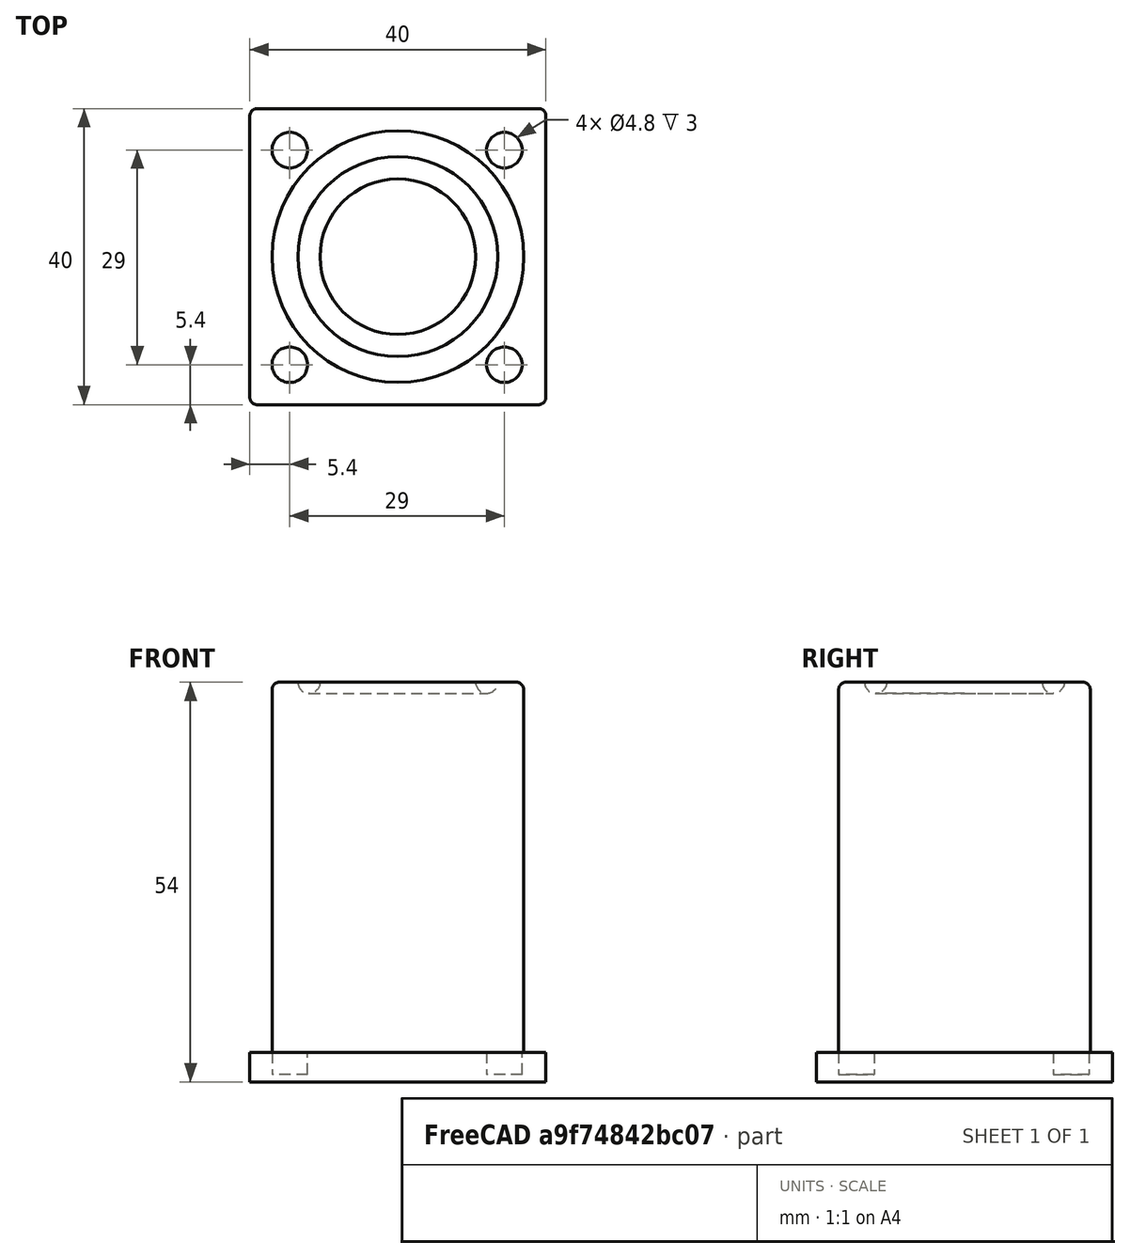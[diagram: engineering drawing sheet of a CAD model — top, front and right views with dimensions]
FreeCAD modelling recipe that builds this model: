
FCSTD DOCUMENT  (FreeCAD 1.0R39319 (Git))
Label: ojt1_t15r03_table_leg
License: All rights reserved
LicenseURL: https://en.wikipedia.org/wiki/All_rights_reserved
objects: Part::Cylinder×5, Part::Cut×2, Part::Fillet×2, Part::Box×1, Part::MultiFuse×1, Part::Torus×1
note: 12 computed .brp shape members not serialized (recipe doc carries the construction recipe); baked Part::Feature solids carry a one-line shape summary decoded from their .brp

FEATURE [Part::Box] Box  label="Cub"
  AttacherType = Attacher::AttachEngine3D
  Height = 4
  Length = 40
  Width = 40
FEATURE [Part::Cylinder] Cylinder  label="Cilindre"
  Angle = 360
  AttacherType = Attacher::AttachEngine3D
  FirstAngle = 0
  Height = 3
  Placement = pos=(5.4,5.4,1) rot=(0,0,1;0rad)
  Radius = 2.4
  SecondAngle = 0
FEATURE [Part::Cylinder] Cylinder001  label="Cilindre001"
  Angle = 360
  AttacherType = Attacher::AttachEngine3D
  FirstAngle = 0
  Height = 3
  Placement = pos=(34.4,5.4,1) rot=(0,0,1;0rad)
  Radius = 2.4
  SecondAngle = 0
FEATURE [Part::Cylinder] Cylinder002  label="Cilindre002"
  Angle = 360
  AttacherType = Attacher::AttachEngine3D
  FirstAngle = 0
  Height = 3
  Placement = pos=(34.4,34.4,1) rot=(0,0,1;0rad)
  Radius = 2.4
  SecondAngle = 0
FEATURE [Part::Cylinder] Cylinder003  label="Cilindre003"
  Angle = 360
  AttacherType = Attacher::AttachEngine3D
  FirstAngle = 0
  Height = 3
  Placement = pos=(5.4,34.4,1) rot=(0,0,1;0rad)
  Radius = 2.4
  SecondAngle = 0
FEATURE [Part::MultiFuse] Fusion
  Refine = true
  Shapes = -> [Cylinder,Cylinder001,Cylinder002,Cylinder003]
FEATURE [Part::Cut] Cut
  Base = -> Box
  Placement = pos=(-20,-20,0) rot=(0,0,1;0rad)
  Refine = true
  Tool = -> Fusion
FEATURE [Part::Cylinder] Cylinder004  label="Cilindre004"
  Angle = 360
  AttacherType = Attacher::AttachEngine3D
  FirstAngle = 0
  Height = 50
  Placement = pos=(0,0,4) rot=(0,0,1;0rad)
  Radius = 17
  SecondAngle = 0
FEATURE [Part::Torus] Torus
  Angle1 = -180
  Angle2 = 180
  Angle3 = 360
  AttacherType = Attacher::AttachEngine3D
  Placement = pos=(0,0,54) rot=(0,0,1;0rad)
  Radius1 = 12
  Radius2 = 1.5
FEATURE [Part::Cut] Cut001
  Base = -> Cylinder004
  Refine = true
  Tool = -> Torus
FEATURE [Part::Fillet] Fillet
  Base = -> Cut001
  EdgeLinks = -> Cut001 [Edge3]
  Edges = 1 edges r=1: [Edge3]
FEATURE [Part::Fillet] Fillet001
  Base = -> Cut
  EdgeLinks = -> Cut [Edge1,Edge3,Edge6,Edge15]
  Edges = 4 edges r=1: [Edge1,Edge3,Edge6,Edge15]
